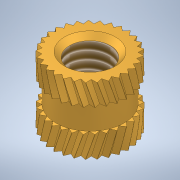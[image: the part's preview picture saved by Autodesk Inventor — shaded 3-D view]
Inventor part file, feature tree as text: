
AUTODESK INVENTOR PART (.ipt)
format: ipt  version: 2022 (Build 260153000, 153)  size: 764,416 bytes
history: native  units: mm
features: sketch x4, revolve x1, loft x1, pattern_circular x1, plane x1, mirror x1, hole x1, chamfer x1, projected_geometry x1
ambient origin geometry x8: Origin, YZ Plane, XZ Plane, XY Plane, X Axis, Y Axis, Z Axis, Center Point
bodies: Solid1 (feature_tree)
feature tree (12):
  revolve  "Revolution1"  [1 undecoded]
  loft  "Loft2"
  pattern_circular  "Circular Pattern2"  [2 undecoded]
  plane  "Work Plane1"
  mirror  "Mirror1"
  hole  "Hole1"  [1 undecoded]
  chamfer  "Chamfer1"  Distance=0.25mm
  sketch  "Sketch1"  dims[d0=2.3mm d1=4.0mm]
  sketch  "Sketch2"  dims[d2=0.25mm d3=1.3mm d4=1.3mm d5=1.3mm]
  projected_geometry  "Projected Loop1"
  sketch  "Sketch3"  dims[d6=90.0deg]
  sketch  "Sketch4"  dims[d16=0.5mm d17=0.25mm d18=0.5mm d19=0.25mm d20=0.0mm d21=90.0deg d22=0.0mm d23=90.0deg d24=0.1mm d25=0.1mm d26=1.745329mm d30=290.0mm d31=360.0deg d33=2.459mm d34=6.0mm d35=6.3mm d36=2.0mm d37=90.0deg d38=8.0mm d39=20.594885mm d40=0.3mm d41=2.0mm d42=45.0deg d43=0.25mm d44=0.25mm]
note: 4 required parameter values undecoded (feature->parameter linkage not recoverable at this tier; creation-order binding heuristic only, values carry confidence <= 0.55)